# Revit family: A_Door_Single Arch Panel
name_source: partatom
category: Doors
units: mm (PartAtom-declared; Revit-internal decimal feet)

## family parameters
Always vertical = Yes
Cut with Voids When Loaded = No
Host = Wall
OmniClass Number = 23.30.10.00
OmniClass Title = Doors
Room Calculation Point = No
Shared = No

## types (1)
- 900Wx2100H
    Analytic Construction = Wooden
    Assembly Code = C1020300
    Clearance = CLEARANCE
    Construction Type Id = DOOR
    Define Thermal Properties by = Schematic Type
    Function = Interior
    Heat Transfer Coefficient (U) = 2.1946 W/(m²·K)
    Height = 2100 mm
    Panel Material = Wood - Birch - Solid Stained Light Low Gloss
    R = 300 mm  [stored 0.984252 ft]
    R2 = 350 mm  [stored 1.14829 ft]
    Solar Heat Gain Coefficient = 0
    Thermal Resistance (R) = 0.4557 (m²·K)/W
    Thickness = 50 mm  [stored 0.164042 ft]
    Trim Material = Paint - Sienna
    Trim Projection Ext = 25 mm  [stored 0.082021 ft]
    Trim Projection Int = 25 mm  [stored 0.082021 ft]
    Trim Width = 50 mm  [stored 0.164042 ft]
    Visual Light Transmittance = 0
    Wall Closure = By host
    Width = 900 mm  [stored 2.95276 ft]

note: [stored X ft] marks values corroborated as IEEE doubles in the binary element streams (Revit-internal decimal feet)

## geometry (parser evidence)
native form markers: Sweep x7
no freeform markers — native parametric forms only
